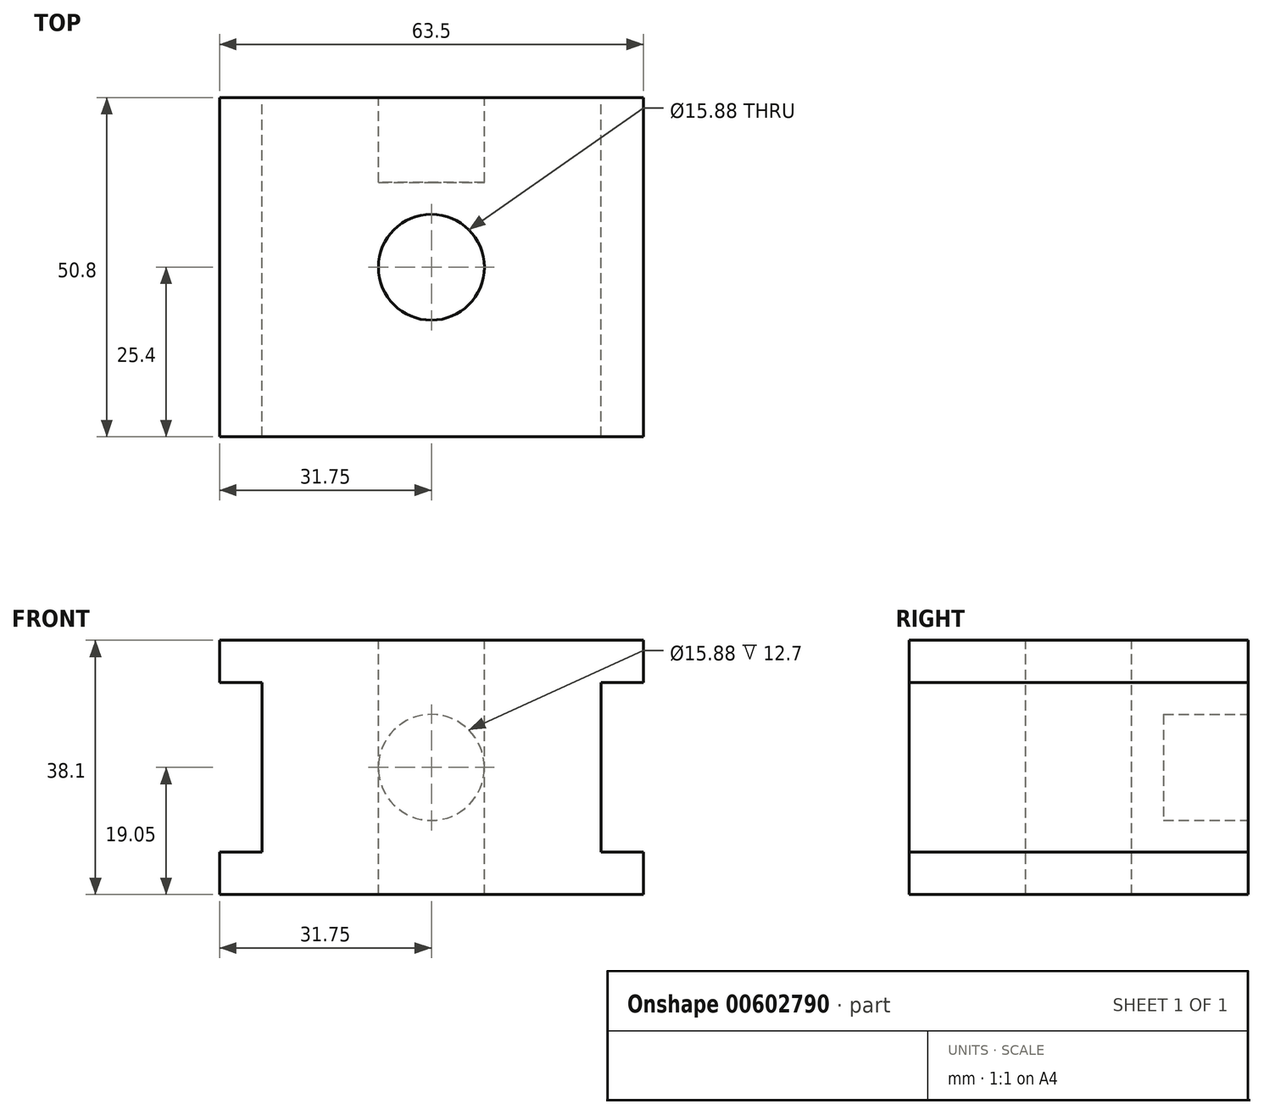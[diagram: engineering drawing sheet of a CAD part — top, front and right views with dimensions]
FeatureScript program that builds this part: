
annotation { "Feature Type Name" : "Feature", "Feature Type Description" : "" }
export const myFeature = defineFeature(function(context is Context, id is Id, definition is map)
    precondition{}
    {
        {
            var Q0;
            Q0=qCreatedBy(makeId("Front.planeOp"),FACE);
            var sketch = newSketch(context, id + "F0", { "sketchPlane" : qUnion([Q0])});
            skLineSegment(sketch, "E0", {"start": v(0, 57.34) * mm, "end": v(0, -63.13) * mm, "construction": true});
            skLineSegment(sketch, "E1", {"start": v(-55.1, 0) * mm, "end": v(53.6, 0) * mm, "construction": true});
            skLineSegment(sketch, "E2.bottom", {"start": v(31.75, -19.05) * mm, "end": v(-31.75, -19.05) * mm});
            skLineSegment(sketch, "E2.top", {"start": v(31.75, 19.05) * mm, "end": v(-31.75, 19.05) * mm});
            skLineSegment(sketch, "E2.left", {"start": v(31.75, -19.05) * mm, "end": v(31.75, 19.05) * mm});
            skLineSegment(sketch, "E2.right", {"start": v(-31.75, -19.05) * mm, "end": v(-31.75, 19.05) * mm});
            skPoint(sketch, "E2.middle", {"position": v(0, 0) * mm});
            skLineSegment(sketch, "E3.bottom", {"start": v(38.1, -12.7) * mm, "end": v(25.4, -12.7) * mm});
            skLineSegment(sketch, "E3.top", {"start": v(38.1, 12.7) * mm, "end": v(25.4, 12.7) * mm});
            skLineSegment(sketch, "E3.left", {"start": v(38.1, -12.7) * mm, "end": v(38.1, 12.7) * mm});
            skLineSegment(sketch, "E3.right", {"start": v(25.4, -12.7) * mm, "end": v(25.4, 12.7) * mm});
            skPoint(sketch, "E3.middle", {"position": v(31.75, 0) * mm});
            skLineSegment(sketch, "E4.MirrorCS", {"start": v(-38.1, -12.7) * mm, "end": v(-38.1, 12.7) * mm});
            skLineSegment(sketch, "E5.MirrorCS", {"start": v(-25.4, -12.7) * mm, "end": v(-25.4, 12.7) * mm});
            skLineSegment(sketch, "E6.MirrorCS", {"start": v(-38.1, -12.7) * mm, "end": v(-25.4, -12.7) * mm});
            skLineSegment(sketch, "E7.MirrorCS", {"start": v(-38.1, 12.7) * mm, "end": v(-25.4, 12.7) * mm});
            skSolve(sketch);
        }
        {
            var Q0;
            {var subQ8=sQuery(id+"F0.wireOp",EDGE,"E2.bottom");Q0=makeQuery(id+"F0.imprint","IMPRINT",FACE,{"disambiguationData":[TD([[makeQuery(id+"F0.imprint","IMPRINT",EDGE,{"derivedFrom":subQ8}),-1.0]])]});}
            extrude(context, id + "F1", {"entities" : qUnion([Q0]), "depth" : 50.8 * mm, "offsetDistance" : 25.4 * mm});
        }
        {
            var Q0;
            Q0=makeQuery(id+"F1.opExtrude","SWEPT_FACE",FACE,{"disambiguationData":[OSD([sQuery(id+"F0.wireOp",EDGE,"E2.top")])]});
            var sketch = newSketch(context, id + "F2", { "sketchPlane" : qUnion([Q0])});
            skCircle(sketch, "E8", {"center": v(0, -25.4) * mm, "radius": 7.94 * mm});
            skPoint(sketch, "E8.centerSnap0", {"position": v(31.75, -25.4) * mm});
            skPoint(sketch, "E8.centerSnap1", {"position": v(0, -50.8) * mm});
            skSolve(sketch);
        }
        {
            var Q0;
            Q0 = qSketchRegion(id + "F2", true);
            extrude(context, id + "F3", {"entities" : qUnion([Q0]), "operationType" : NewBodyOperationType.REMOVE, "endBound" : BoundingType.THROUGH_ALL, "oppositeDirection" : true, "depth" : 25.4 * mm, "offsetDistance" : 25.4 * mm});
        }
        {
            var Q0;
            Q0=makeQuery(id+"F1.opExtrude","CAP_FACE",FACE,{"disambiguationData":[OSD([sQuery(id+"F0.wireOp",EDGE,"E2.bottom"),sQuery(id+"F0.wireOp",EDGE,"E2.top"),sQuery(id+"F0.wireOp",EDGE,"E2.left"),sQuery(id+"F0.wireOp",EDGE,"E2.right"),sQuery(id+"F0.wireOp",EDGE,"E3.bottom"),sQuery(id+"F0.wireOp",EDGE,"E3.top"),sQuery(id+"F0.wireOp",EDGE,"E3.right"),sQuery(id+"F0.wireOp",EDGE,"E5.MirrorCS"),sQuery(id+"F0.wireOp",EDGE,"E6.MirrorCS"),sQuery(id+"F0.wireOp",EDGE,"E7.MirrorCS")])],"isStart":true});
            var sketch = newSketch(context, id + "F4", { "sketchPlane" : qUnion([Q0])});
            skCircle(sketch, "E9", {"center": v(0, 0) * mm, "radius": 7.94 * mm});
            skSolve(sketch);
        }
        {
            var Q0;
            Q0 = qSketchRegion(id + "F4", true);
            extrude(context, id + "F5", {"entities" : qUnion([Q0]), "operationType" : NewBodyOperationType.REMOVE, "oppositeDirection" : true, "depth" : 12.7 * mm, "offsetDistance" : 25.4 * mm});
        }
    });
